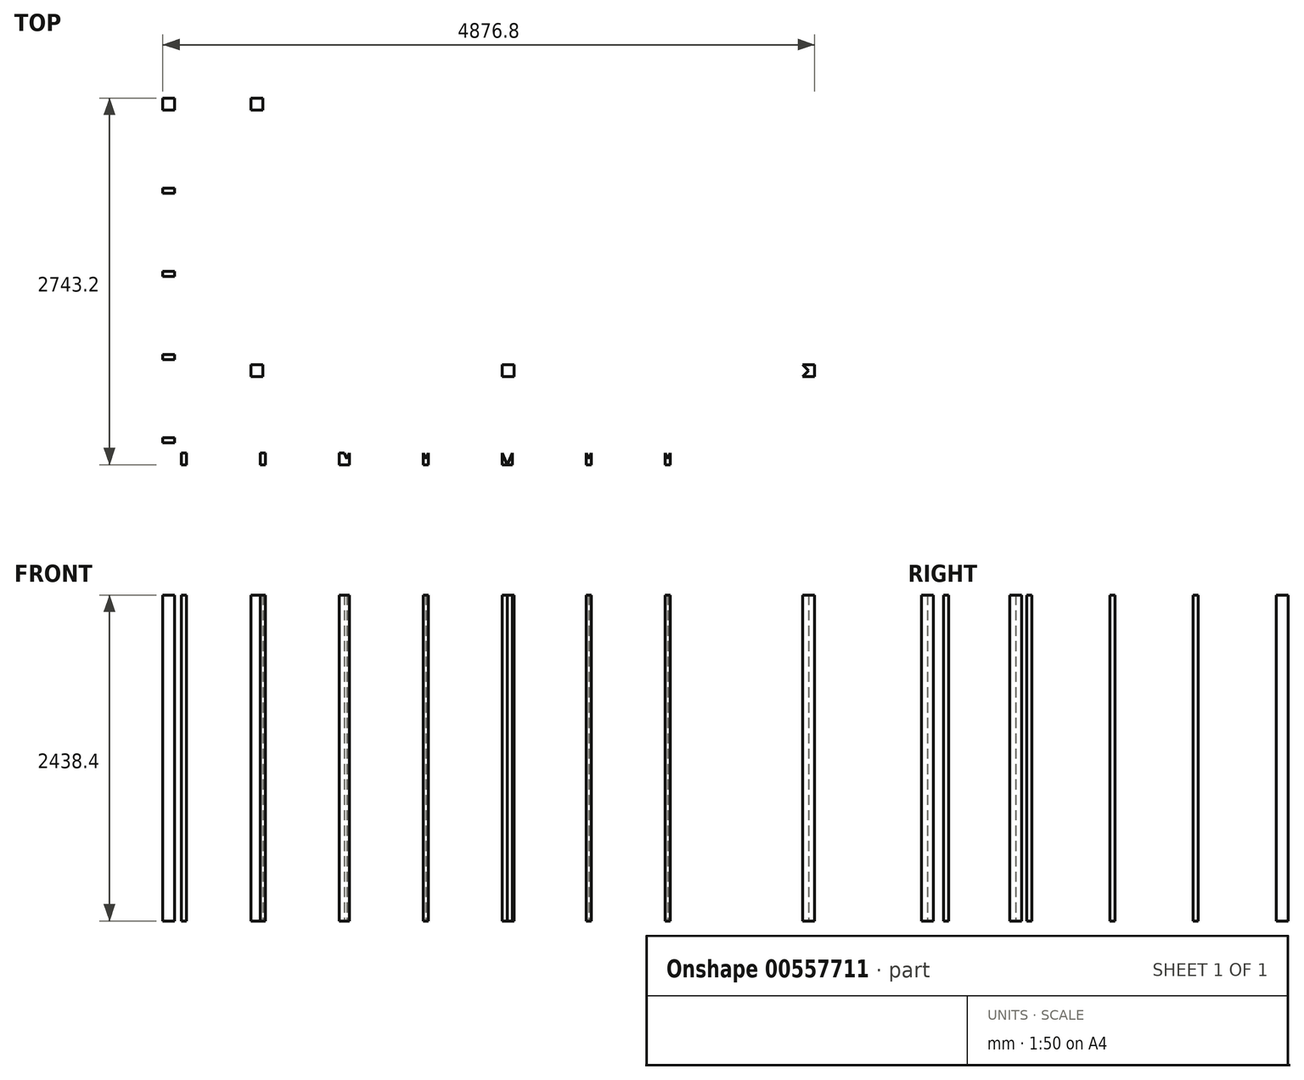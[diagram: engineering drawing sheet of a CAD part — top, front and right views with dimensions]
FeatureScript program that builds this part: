
annotation { "Feature Type Name" : "Feature", "Feature Type Description" : "" }
export const myFeature = defineFeature(function(context is Context, id is Id, definition is map)
    precondition{}
    {
        {
            var Q0;
            Q0=qCreatedBy(makeId("Top.planeOp"),FACE);
            var sketch = newSketch(context, id + "F0", { "sketchPlane" : qUnion([Q0])});
            skLineSegment(sketch, "E0.bottom", {"start": v(-518.2, -3048.88) * mm, "end": v(-518.2, -3086.98) * mm});
            skLineSegment(sketch, "E0.top", {"start": v(-429.3, -3048.88) * mm, "end": v(-429.3, -3086.98) * mm});
            skLineSegment(sketch, "E0.left", {"start": v(-518.2, -3048.88) * mm, "end": v(-429.3, -3048.88) * mm});
            skLineSegment(sketch, "E0.right", {"start": v(-518.2, -3086.98) * mm, "end": v(-429.3, -3086.98) * mm});
            skLineSegment(sketch, "E1", {"start": v(-518.2, -3086.98) * mm, "end": v(-429.3, -3048.88) * mm});
            skLineSegment(sketch, "E2", {"start": v(-518.2, -3048.88) * mm, "end": v(-429.3, -3086.98) * mm});
            skLineSegment(sketch, "E3.bottom", {"start": v(0, -673.1) * mm, "end": v(0, -711.2) * mm});
            skLineSegment(sketch, "E3.top", {"start": v(88.9, -673.1) * mm, "end": v(88.9, -711.2) * mm});
            skLineSegment(sketch, "E3.left", {"start": v(0, -673.1) * mm, "end": v(88.9, -673.1) * mm});
            skLineSegment(sketch, "E3.right", {"start": v(0, -711.2) * mm, "end": v(88.9, -711.2) * mm});
            skLineSegment(sketch, "E4", {"start": v(0, -711.2) * mm, "end": v(88.9, -673.1) * mm});
            skLineSegment(sketch, "E5", {"start": v(0, -673.1) * mm, "end": v(88.9, -711.2) * mm});
            skLineSegment(sketch, "E6.bottom", {"start": v(-839.1, -3188.58) * mm, "end": v(-839.1, -3277.48) * mm});
            skLineSegment(sketch, "E6.top", {"start": v(-801, -3188.58) * mm, "end": v(-801, -3277.48) * mm});
            skLineSegment(sketch, "E6.left", {"start": v(-839.1, -3188.58) * mm, "end": v(-801, -3188.58) * mm});
            skLineSegment(sketch, "E6.right", {"start": v(-839.1, -3277.48) * mm, "end": v(-801, -3277.48) * mm});
            skLineSegment(sketch, "E7", {"start": v(-839.1, -3277.48) * mm, "end": v(-801, -3188.58) * mm});
            skLineSegment(sketch, "E8", {"start": v(-839.1, -3188.58) * mm, "end": v(-801, -3277.48) * mm});
            skLineSegment(sketch, "E9.bottom", {"start": v(139.7, -2654.3) * mm, "end": v(139.7, -2743.2) * mm});
            skLineSegment(sketch, "E9.top", {"start": v(177.8, -2654.3) * mm, "end": v(177.8, -2743.2) * mm});
            skLineSegment(sketch, "E9.left", {"start": v(139.7, -2654.3) * mm, "end": v(177.8, -2654.3) * mm});
            skLineSegment(sketch, "E9.right", {"start": v(139.7, -2743.2) * mm, "end": v(177.8, -2743.2) * mm});
            skLineSegment(sketch, "E10", {"start": v(139.7, -2743.2) * mm, "end": v(177.8, -2654.3) * mm});
            skLineSegment(sketch, "E11", {"start": v(139.7, -2654.3) * mm, "end": v(177.8, -2743.2) * mm});
            skLineSegment(sketch, "E12.0.1.0", {"start": v(730.25, -2654.3) * mm, "end": v(730.25, -2743.2) * mm});
            skLineSegment(sketch, "E12.0.1.1", {"start": v(730.25, -2743.2) * mm, "end": v(768.35, -2654.3) * mm});
            skLineSegment(sketch, "E12.0.1.2", {"start": v(730.25, -2654.3) * mm, "end": v(768.35, -2654.3) * mm});
            skLineSegment(sketch, "E12.0.1.3", {"start": v(730.25, -2743.2) * mm, "end": v(768.35, -2743.2) * mm});
            skLineSegment(sketch, "E12.0.1.4", {"start": v(730.25, -2654.3) * mm, "end": v(768.35, -2743.2) * mm});
            skLineSegment(sketch, "E12.0.1.5", {"start": v(768.35, -2654.3) * mm, "end": v(768.35, -2743.2) * mm});
            skLineSegment(sketch, "E12.0.2.0", {"start": v(1320.8, -2654.3) * mm, "end": v(1320.8, -2743.2) * mm});
            skLineSegment(sketch, "E12.0.2.1", {"start": v(1320.8, -2743.2) * mm, "end": v(1358.9, -2654.3) * mm});
            skLineSegment(sketch, "E12.0.2.2", {"start": v(1320.8, -2654.3) * mm, "end": v(1358.9, -2654.3) * mm});
            skLineSegment(sketch, "E12.0.2.3", {"start": v(1320.8, -2743.2) * mm, "end": v(1358.9, -2743.2) * mm});
            skLineSegment(sketch, "E12.0.2.4", {"start": v(1320.8, -2654.3) * mm, "end": v(1358.9, -2743.2) * mm});
            skLineSegment(sketch, "E12.0.2.5", {"start": v(1358.9, -2654.3) * mm, "end": v(1358.9, -2743.2) * mm});
            skLineSegment(sketch, "E12.direction1", {"start": v(177.8, -2792) * mm, "end": v(177.8, -2743.2) * mm, "construction": true});
            skLineSegment(sketch, "E12.direction2", {"start": v(177.8, -2743.2) * mm, "end": v(768.35, -2743.2) * mm, "construction": true});
            skLineSegment(sketch, "E13.bottom", {"start": v(139.7, -2654.3) * mm, "end": v(139.7, -2641.6) * mm});
            skLineSegment(sketch, "E13.top", {"start": v(1358.9, -2654.3) * mm, "end": v(1358.9, -2641.6) * mm});
            skLineSegment(sketch, "E13.left", {"start": v(139.7, -2654.3) * mm, "end": v(1358.9, -2654.3) * mm});
            skLineSegment(sketch, "E13.right", {"start": v(139.7, -2641.6) * mm, "end": v(1358.9, -2641.6) * mm});
            skLineSegment(sketch, "E14.0.1.0", {"start": v(1949.45, -2654.3) * mm, "end": v(1987.55, -2743.2) * mm});
            skLineSegment(sketch, "E14.0.1.1", {"start": v(1358.9, -2654.3) * mm, "end": v(2578.1, -2654.3) * mm});
            skLineSegment(sketch, "E14.0.1.2", {"start": v(2540, -2654.3) * mm, "end": v(2540, -2743.2) * mm});
            skLineSegment(sketch, "E14.0.1.3", {"start": v(1358.9, -2641.6) * mm, "end": v(2578.1, -2641.6) * mm});
            skLineSegment(sketch, "E14.0.1.4", {"start": v(1397, -2743.2) * mm, "end": v(1987.55, -2743.2) * mm, "construction": true});
            skLineSegment(sketch, "E14.0.1.5", {"start": v(1987.55, -2654.3) * mm, "end": v(1987.55, -2743.2) * mm});
            skLineSegment(sketch, "E14.0.1.6", {"start": v(1949.45, -2654.3) * mm, "end": v(1949.45, -2743.2) * mm});
            skLineSegment(sketch, "E14.0.1.8", {"start": v(2540, -2743.2) * mm, "end": v(2578.1, -2654.3) * mm});
            skLineSegment(sketch, "E14.0.1.9", {"start": v(2578.1, -2654.3) * mm, "end": v(2578.1, -2743.2) * mm});
            skLineSegment(sketch, "E14.0.1.10", {"start": v(1949.45, -2743.2) * mm, "end": v(1987.55, -2654.3) * mm});
            skLineSegment(sketch, "E14.0.1.11", {"start": v(2540, -2654.3) * mm, "end": v(2578.1, -2743.2) * mm});
            skLineSegment(sketch, "E14.0.1.12", {"start": v(1358.9, -2654.3) * mm, "end": v(1397, -2743.2) * mm});
            skLineSegment(sketch, "E14.0.1.13", {"start": v(1397, -2654.3) * mm, "end": v(1397, -2743.2) * mm});
            skLineSegment(sketch, "E14.0.1.14", {"start": v(1358.9, -2743.2) * mm, "end": v(1397, -2654.3) * mm});
            skLineSegment(sketch, "E14.0.1.15", {"start": v(1949.45, -2654.3) * mm, "end": v(1987.55, -2654.3) * mm});
            skLineSegment(sketch, "E14.0.1.16", {"start": v(1949.45, -2743.2) * mm, "end": v(1987.55, -2743.2) * mm});
            skLineSegment(sketch, "E14.0.1.17", {"start": v(1358.9, -2654.3) * mm, "end": v(1397, -2654.3) * mm});
            skLineSegment(sketch, "E14.0.1.18", {"start": v(2540, -2654.3) * mm, "end": v(2578.1, -2654.3) * mm});
            skLineSegment(sketch, "E14.0.1.19", {"start": v(2540, -2743.2) * mm, "end": v(2578.1, -2743.2) * mm});
            skLineSegment(sketch, "E14.0.1.20", {"start": v(1358.9, -2743.2) * mm, "end": v(1397, -2743.2) * mm});
            skLineSegment(sketch, "E14.0.1.22", {"start": v(2578.1, -2654.3) * mm, "end": v(2578.1, -2641.6) * mm});
            skLineSegment(sketch, "E14.0.1.23", {"start": v(1397, -2792) * mm, "end": v(1397, -2743.2) * mm, "construction": true});
            skLineSegment(sketch, "E14.0.2.0", {"start": v(3168.65, -2654.3) * mm, "end": v(3206.75, -2743.2) * mm});
            skLineSegment(sketch, "E14.0.2.1", {"start": v(2578.1, -2654.3) * mm, "end": v(3797.3, -2654.3) * mm});
            skLineSegment(sketch, "E14.0.2.2", {"start": v(3759.2, -2654.3) * mm, "end": v(3759.2, -2743.2) * mm});
            skLineSegment(sketch, "E14.0.2.3", {"start": v(2578.1, -2641.6) * mm, "end": v(3797.3, -2641.6) * mm});
            skLineSegment(sketch, "E14.0.2.4", {"start": v(2616.2, -2743.2) * mm, "end": v(3206.75, -2743.2) * mm, "construction": true});
            skLineSegment(sketch, "E14.0.2.5", {"start": v(3206.75, -2654.3) * mm, "end": v(3206.75, -2743.2) * mm});
            skLineSegment(sketch, "E14.0.2.6", {"start": v(3168.65, -2654.3) * mm, "end": v(3168.65, -2743.2) * mm});
            skLineSegment(sketch, "E14.0.2.7", {"start": v(2578.1, -2654.3) * mm, "end": v(2578.1, -2743.2) * mm});
            skLineSegment(sketch, "E14.0.2.8", {"start": v(3759.2, -2743.2) * mm, "end": v(3797.3, -2654.3) * mm});
            skLineSegment(sketch, "E14.0.2.9", {"start": v(3797.3, -2654.3) * mm, "end": v(3797.3, -2743.2) * mm});
            skLineSegment(sketch, "E14.0.2.10", {"start": v(3168.65, -2743.2) * mm, "end": v(3206.75, -2654.3) * mm});
            skLineSegment(sketch, "E14.0.2.11", {"start": v(3759.2, -2654.3) * mm, "end": v(3797.3, -2743.2) * mm});
            skLineSegment(sketch, "E14.0.2.12", {"start": v(2578.1, -2654.3) * mm, "end": v(2616.2, -2743.2) * mm});
            skLineSegment(sketch, "E14.0.2.13", {"start": v(2616.2, -2654.3) * mm, "end": v(2616.2, -2743.2) * mm});
            skLineSegment(sketch, "E14.0.2.14", {"start": v(2578.1, -2743.2) * mm, "end": v(2616.2, -2654.3) * mm});
            skLineSegment(sketch, "E14.0.2.15", {"start": v(3168.65, -2654.3) * mm, "end": v(3206.75, -2654.3) * mm});
            skLineSegment(sketch, "E14.0.2.16", {"start": v(3168.65, -2743.2) * mm, "end": v(3206.75, -2743.2) * mm});
            skLineSegment(sketch, "E14.0.2.17", {"start": v(2578.1, -2654.3) * mm, "end": v(2616.2, -2654.3) * mm});
            skLineSegment(sketch, "E14.0.2.18", {"start": v(3759.2, -2654.3) * mm, "end": v(3797.3, -2654.3) * mm});
            skLineSegment(sketch, "E14.0.2.19", {"start": v(3759.2, -2743.2) * mm, "end": v(3797.3, -2743.2) * mm});
            skLineSegment(sketch, "E14.0.2.20", {"start": v(2578.1, -2743.2) * mm, "end": v(2616.2, -2743.2) * mm});
            skLineSegment(sketch, "E14.0.2.21", {"start": v(2578.1, -2654.3) * mm, "end": v(2578.1, -2641.6) * mm});
            skLineSegment(sketch, "E14.0.2.22", {"start": v(3797.3, -2654.3) * mm, "end": v(3797.3, -2641.6) * mm});
            skLineSegment(sketch, "E14.0.2.23", {"start": v(2616.2, -2792) * mm, "end": v(2616.2, -2743.2) * mm, "construction": true});
            skLineSegment(sketch, "E14.direction1", {"start": v(1358.9, -2743.2) * mm, "end": v(1358.9, -2667) * mm, "construction": true});
            skLineSegment(sketch, "E14.direction2", {"start": v(1358.9, -2743.2) * mm, "end": v(2578.1, -2743.2) * mm, "construction": true});
            skCircle(sketch, "E15", {"center": v(4876.8, -2804.36) * mm, "radius": 228.6 * mm});
            skLineSegment(sketch, "E16.bottom", {"start": v(660.4, 0) * mm, "end": v(749.3, 0) * mm});
            skLineSegment(sketch, "E16.top", {"start": v(660.4, -88.9) * mm, "end": v(749.3, -88.9) * mm});
            skLineSegment(sketch, "E16.left", {"start": v(660.4, 0) * mm, "end": v(660.4, -88.9) * mm});
            skLineSegment(sketch, "E16.right", {"start": v(749.3, 0) * mm, "end": v(749.3, -88.9) * mm});
            skLineSegment(sketch, "E17", {"start": v(660.4, -88.9) * mm, "end": v(749.3, 0) * mm});
            skLineSegment(sketch, "E18", {"start": v(660.4, 0) * mm, "end": v(749.3, -88.9) * mm});
            skLineSegment(sketch, "E19.bottom", {"start": v(2540, -1993.9) * mm, "end": v(2628.9, -1993.9) * mm});
            skLineSegment(sketch, "E19.top", {"start": v(2540, -2082.8) * mm, "end": v(2628.9, -2082.8) * mm});
            skLineSegment(sketch, "E19.left", {"start": v(2540, -1993.9) * mm, "end": v(2540, -2082.8) * mm});
            skLineSegment(sketch, "E19.right", {"start": v(2628.9, -1993.9) * mm, "end": v(2628.9, -2082.8) * mm});
            skLineSegment(sketch, "E20", {"start": v(2540, -2082.8) * mm, "end": v(2628.9, -1993.9) * mm});
            skLineSegment(sketch, "E21", {"start": v(2540, -1993.9) * mm, "end": v(2628.9, -2082.8) * mm});
            skLineSegment(sketch, "E22.bottom", {"start": v(6053.75, -1993.9) * mm, "end": v(6142.65, -1993.9) * mm});
            skLineSegment(sketch, "E22.top", {"start": v(6053.75, -2082.8) * mm, "end": v(6142.65, -2082.8) * mm});
            skLineSegment(sketch, "E22.left", {"start": v(6053.75, -1993.9) * mm, "end": v(6053.75, -2082.8) * mm});
            skLineSegment(sketch, "E22.right", {"start": v(6142.65, -1993.9) * mm, "end": v(6142.65, -2082.8) * mm});
            skLineSegment(sketch, "E23", {"start": v(6053.75, -2082.8) * mm, "end": v(6142.65, -1993.9) * mm});
            skLineSegment(sketch, "E24", {"start": v(6053.75, -1993.9) * mm, "end": v(6142.65, -2082.8) * mm});
            skLineSegment(sketch, "E25.bottom", {"start": v(114.3, -2628.9) * mm, "end": v(-114.3, -2628.9) * mm});
            skLineSegment(sketch, "E25.top", {"start": v(114.3, -2857.5) * mm, "end": v(-114.3, -2857.5) * mm});
            skLineSegment(sketch, "E25.left", {"start": v(114.3, -2628.9) * mm, "end": v(114.3, -2857.5) * mm});
            skLineSegment(sketch, "E25.right", {"start": v(-114.3, -2628.9) * mm, "end": v(-114.3, -2857.5) * mm});
            skLineSegment(sketch, "E26.bottom", {"start": v(4787.9, -1371.6) * mm, "end": v(4787.9, -1409.7) * mm});
            skLineSegment(sketch, "E26.top", {"start": v(4876.8, -1371.6) * mm, "end": v(4876.8, -1409.7) * mm});
            skLineSegment(sketch, "E26.left", {"start": v(4787.9, -1371.6) * mm, "end": v(4876.8, -1371.6) * mm});
            skLineSegment(sketch, "E26.right", {"start": v(4787.9, -1409.7) * mm, "end": v(4876.8, -1409.7) * mm});
            skLineSegment(sketch, "E27", {"start": v(4787.9, -1409.7) * mm, "end": v(4876.8, -1371.6) * mm});
            skLineSegment(sketch, "E28", {"start": v(4787.9, -1371.6) * mm, "end": v(4876.8, -1409.7) * mm});
            skLineSegment(sketch, "E29.bottom", {"start": v(4787.9, -571.5) * mm, "end": v(4787.9, -609.6) * mm});
            skLineSegment(sketch, "E29.top", {"start": v(4876.8, -571.5) * mm, "end": v(4876.8, -609.6) * mm});
            skLineSegment(sketch, "E29.left", {"start": v(4787.9, -571.5) * mm, "end": v(4876.8, -571.5) * mm});
            skLineSegment(sketch, "E29.right", {"start": v(4787.9, -609.6) * mm, "end": v(4876.8, -609.6) * mm});
            skLineSegment(sketch, "E30", {"start": v(4787.9, -609.6) * mm, "end": v(4876.8, -571.5) * mm});
            skLineSegment(sketch, "E31", {"start": v(4787.9, -571.5) * mm, "end": v(4876.8, -609.6) * mm});
            skLineSegment(sketch, "E32.bottom", {"start": v(5923.7, -2715.46) * mm, "end": v(5923.7, -2804.36) * mm});
            skLineSegment(sketch, "E32.top", {"start": v(5961.8, -2715.46) * mm, "end": v(5961.8, -2804.36) * mm});
            skLineSegment(sketch, "E32.left", {"start": v(5923.7, -2715.46) * mm, "end": v(5961.8, -2715.46) * mm});
            skLineSegment(sketch, "E32.right", {"start": v(5923.7, -2804.36) * mm, "end": v(5961.8, -2804.36) * mm});
            skLineSegment(sketch, "E33", {"start": v(5923.7, -2804.36) * mm, "end": v(5961.8, -2715.46) * mm});
            skLineSegment(sketch, "E34", {"start": v(5923.7, -2715.46) * mm, "end": v(5961.8, -2804.36) * mm});
            skLineSegment(sketch, "E35.bottom", {"start": v(4787.9, -1638.3) * mm, "end": v(4787.9, -1676.4) * mm});
            skLineSegment(sketch, "E35.top", {"start": v(4876.8, -1638.3) * mm, "end": v(4876.8, -1676.4) * mm});
            skLineSegment(sketch, "E35.left", {"start": v(4787.9, -1638.3) * mm, "end": v(4876.8, -1638.3) * mm});
            skLineSegment(sketch, "E35.right", {"start": v(4787.9, -1676.4) * mm, "end": v(4876.8, -1676.4) * mm});
            skLineSegment(sketch, "E36", {"start": v(4787.9, -1676.4) * mm, "end": v(4876.8, -1638.3) * mm});
            skLineSegment(sketch, "E37", {"start": v(4787.9, -1638.3) * mm, "end": v(4876.8, -1676.4) * mm});
            skLineSegment(sketch, "E38.bottom", {"start": v(7014.46, -3056.69) * mm, "end": v(7204.96, -3056.69) * mm});
            skLineSegment(sketch, "E38.top", {"start": v(6442.96, -3818.69) * mm, "end": v(7103.36, -3818.69) * mm});
            skLineSegment(sketch, "E38.left", {"start": v(6442.96, -3628.19) * mm, "end": v(6442.96, -3818.69) * mm});
            skLineSegment(sketch, "E38.right", {"start": v(7204.96, -3056.69) * mm, "end": v(7204.96, -3717.09) * mm});
            skLineSegment(sketch, "E39", {"start": v(6442.96, -3628.19) * mm, "end": v(7014.46, -3056.69) * mm});
            skLineSegment(sketch, "E40", {"start": v(7204.96, -3717.09) * mm, "end": v(7103.36, -3818.69) * mm});
            skLineSegment(sketch, "E41.bottom", {"start": v(4554.32, -1919.19) * mm, "end": v(4744.82, -1919.19) * mm});
            skLineSegment(sketch, "E41.top", {"start": v(3982.82, -2681.19) * mm, "end": v(4643.22, -2681.19) * mm});
            skLineSegment(sketch, "E41.left", {"start": v(3982.82, -2490.69) * mm, "end": v(3982.82, -2681.19) * mm});
            skLineSegment(sketch, "E41.right", {"start": v(4744.82, -1919.19) * mm, "end": v(4744.82, -2579.59) * mm});
            skLineSegment(sketch, "E42", {"start": v(3982.82, -2490.69) * mm, "end": v(4554.32, -1919.19) * mm});
            skLineSegment(sketch, "E43", {"start": v(4744.82, -2579.59) * mm, "end": v(4643.22, -2681.19) * mm});
            skLineSegment(sketch, "E44.bottom", {"start": v(4787.9, 0) * mm, "end": v(4787.9, -38.1) * mm});
            skLineSegment(sketch, "E44.top", {"start": v(4876.8, 0) * mm, "end": v(4876.8, -38.1) * mm});
            skLineSegment(sketch, "E44.left", {"start": v(4787.9, 0) * mm, "end": v(4876.8, 0) * mm});
            skLineSegment(sketch, "E44.right", {"start": v(4787.9, -38.1) * mm, "end": v(4876.8, -38.1) * mm});
            skLineSegment(sketch, "E45", {"start": v(4787.9, -38.1) * mm, "end": v(4876.8, 0) * mm});
            skLineSegment(sketch, "E46", {"start": v(4787.9, 0) * mm, "end": v(4876.8, -38.1) * mm});
            skLineSegment(sketch, "E47.bottom", {"start": v(0, 0) * mm, "end": v(88.9, 0) * mm});
            skLineSegment(sketch, "E47.top", {"start": v(0, -88.9) * mm, "end": v(88.9, -88.9) * mm});
            skLineSegment(sketch, "E47.left", {"start": v(0, 0) * mm, "end": v(0, -88.9) * mm});
            skLineSegment(sketch, "E47.right", {"start": v(88.9, 0) * mm, "end": v(88.9, -88.9) * mm});
            skLineSegment(sketch, "E48", {"start": v(0, -88.9) * mm, "end": v(88.9, 0) * mm});
            skLineSegment(sketch, "E49", {"start": v(0, 0) * mm, "end": v(88.9, -88.9) * mm});
            skLineSegment(sketch, "E50", {"start": v(-1165.05, -2735.16) * mm, "end": v(-1073.4, -2444.46) * mm});
            skLineSegment(sketch, "E51", {"start": v(-1073.4, -2444.46) * mm, "end": v(-1049.17, -2452.1) * mm});
            skLineSegment(sketch, "E52", {"start": v(-1049.17, -2452.1) * mm, "end": v(-1140.82, -2742.8) * mm});
            skLineSegment(sketch, "E53", {"start": v(-1140.82, -2742.8) * mm, "end": v(-1165.05, -2735.16) * mm});
            skLineSegment(sketch, "E54", {"start": v(-1140.82, -2742.8) * mm, "end": v(-1049.17, -3033.49) * mm});
            skLineSegment(sketch, "E55", {"start": v(-1049.17, -3033.49) * mm, "end": v(-1073.4, -3041.13) * mm});
            skLineSegment(sketch, "E56", {"start": v(-1073.4, -3041.13) * mm, "end": v(-1165.05, -2750.43) * mm});
            skLineSegment(sketch, "E57", {"start": v(-1165.05, -2750.43) * mm, "end": v(-1140.82, -2742.8) * mm});
            skLineSegment(sketch, "E58", {"start": v(-1165.05, -2735.16) * mm, "end": v(-1165.05, -2750.43) * mm});
            skLineSegment(sketch, "E59", {"start": v(-1140.82, -2742.8) * mm, "end": v(-1165.05, -2742.8) * mm, "construction": true});
            skLineSegment(sketch, "E60", {"start": v(0, -370.85) * mm, "end": v(91.66, -80.16) * mm});
            skLineSegment(sketch, "E61", {"start": v(91.66, -80.16) * mm, "end": v(115.88, -87.8) * mm});
            skLineSegment(sketch, "E62", {"start": v(115.88, -87.8) * mm, "end": v(24.22, -378.5) * mm});
            skLineSegment(sketch, "E63", {"start": v(24.22, -378.5) * mm, "end": v(0, -370.85) * mm});
            skLineSegment(sketch, "E64", {"start": v(24.22, -378.5) * mm, "end": v(115.88, -669.19) * mm});
            skLineSegment(sketch, "E65", {"start": v(115.88, -669.19) * mm, "end": v(91.66, -676.82) * mm});
            skLineSegment(sketch, "E66", {"start": v(91.66, -676.82) * mm, "end": v(0, -386.13) * mm});
            skLineSegment(sketch, "E67", {"start": v(0, -386.13) * mm, "end": v(24.22, -378.5) * mm});
            skLineSegment(sketch, "E68", {"start": v(0, -370.85) * mm, "end": v(0, -386.13) * mm});
            skLineSegment(sketch, "E69", {"start": v(24.22, -378.5) * mm, "end": v(0, -378.5) * mm, "construction": true});
            skLineSegment(sketch, "E70.bottom", {"start": v(0, -1295.4) * mm, "end": v(0, -1333.5) * mm});
            skLineSegment(sketch, "E70.top", {"start": v(88.9, -1295.4) * mm, "end": v(88.9, -1333.5) * mm});
            skLineSegment(sketch, "E70.left", {"start": v(0, -1295.4) * mm, "end": v(88.9, -1295.4) * mm});
            skLineSegment(sketch, "E70.right", {"start": v(0, -1333.5) * mm, "end": v(88.9, -1333.5) * mm});
            skLineSegment(sketch, "E71", {"start": v(0, -1333.5) * mm, "end": v(88.9, -1295.4) * mm});
            skLineSegment(sketch, "E72", {"start": v(0, -1295.4) * mm, "end": v(88.9, -1333.5) * mm});
            skLineSegment(sketch, "E73.bottom", {"start": v(0, -1917.7) * mm, "end": v(0, -1955.8) * mm});
            skLineSegment(sketch, "E73.top", {"start": v(88.9, -1917.7) * mm, "end": v(88.9, -1955.8) * mm});
            skLineSegment(sketch, "E73.left", {"start": v(0, -1917.7) * mm, "end": v(88.9, -1917.7) * mm});
            skLineSegment(sketch, "E73.right", {"start": v(0, -1955.8) * mm, "end": v(88.9, -1955.8) * mm});
            skLineSegment(sketch, "E74", {"start": v(0, -1955.8) * mm, "end": v(88.9, -1917.7) * mm});
            skLineSegment(sketch, "E75", {"start": v(0, -1917.7) * mm, "end": v(88.9, -1955.8) * mm});
            skLineSegment(sketch, "E76.bottom", {"start": v(0, -2540) * mm, "end": v(0, -2578.1) * mm});
            skLineSegment(sketch, "E76.top", {"start": v(88.9, -2540) * mm, "end": v(88.9, -2578.1) * mm});
            skLineSegment(sketch, "E76.left", {"start": v(0, -2540) * mm, "end": v(88.9, -2540) * mm});
            skLineSegment(sketch, "E76.right", {"start": v(0, -2578.1) * mm, "end": v(88.9, -2578.1) * mm});
            skLineSegment(sketch, "E77", {"start": v(0, -2578.1) * mm, "end": v(88.9, -2540) * mm});
            skLineSegment(sketch, "E78", {"start": v(0, -2540) * mm, "end": v(88.9, -2578.1) * mm});
            skLineSegment(sketch, "E79.0.1.0", {"start": v(0, -993.15) * mm, "end": v(91.66, -702.46) * mm});
            skLineSegment(sketch, "E79.0.1.1", {"start": v(115.88, -710.1) * mm, "end": v(24.22, -1000.8) * mm});
            skLineSegment(sketch, "E79.0.1.2", {"start": v(24.22, -1000.8) * mm, "end": v(115.88, -1291.49) * mm});
            skLineSegment(sketch, "E79.0.1.3", {"start": v(91.66, -1299.12) * mm, "end": v(0, -1008.43) * mm});
            skLineSegment(sketch, "E79.0.1.4", {"start": v(24.22, -1000.8) * mm, "end": v(0, -993.15) * mm});
            skLineSegment(sketch, "E79.0.1.5", {"start": v(0, -1008.43) * mm, "end": v(24.22, -1000.8) * mm});
            skLineSegment(sketch, "E79.0.1.6", {"start": v(91.66, -702.46) * mm, "end": v(115.88, -710.1) * mm});
            skLineSegment(sketch, "E79.0.1.7", {"start": v(115.88, -1291.49) * mm, "end": v(91.66, -1299.12) * mm});
            skLineSegment(sketch, "E79.0.2.0", {"start": v(0, -1615.45) * mm, "end": v(91.66, -1324.76) * mm});
            skLineSegment(sketch, "E79.0.2.1", {"start": v(115.88, -1332.4) * mm, "end": v(24.22, -1623.1) * mm});
            skLineSegment(sketch, "E79.0.2.2", {"start": v(24.22, -1623.1) * mm, "end": v(115.88, -1913.79) * mm});
            skLineSegment(sketch, "E79.0.2.3", {"start": v(91.66, -1921.42) * mm, "end": v(0, -1630.73) * mm});
            skLineSegment(sketch, "E79.0.2.4", {"start": v(24.22, -1623.1) * mm, "end": v(0, -1615.45) * mm});
            skLineSegment(sketch, "E79.0.2.5", {"start": v(0, -1630.73) * mm, "end": v(24.22, -1623.1) * mm});
            skLineSegment(sketch, "E79.0.2.6", {"start": v(91.66, -1324.76) * mm, "end": v(115.88, -1332.4) * mm});
            skLineSegment(sketch, "E79.0.2.7", {"start": v(115.88, -1913.79) * mm, "end": v(91.66, -1921.42) * mm});
            skLineSegment(sketch, "E79.0.3.0", {"start": v(0, -2237.75) * mm, "end": v(91.66, -1947.06) * mm});
            skLineSegment(sketch, "E79.0.3.1", {"start": v(115.88, -1954.7) * mm, "end": v(24.22, -2245.4) * mm});
            skLineSegment(sketch, "E79.0.3.2", {"start": v(24.22, -2245.4) * mm, "end": v(115.88, -2536.09) * mm});
            skLineSegment(sketch, "E79.0.3.3", {"start": v(91.66, -2543.72) * mm, "end": v(0, -2253.03) * mm});
            skLineSegment(sketch, "E79.0.3.4", {"start": v(24.22, -2245.4) * mm, "end": v(0, -2237.75) * mm});
            skLineSegment(sketch, "E79.0.3.5", {"start": v(0, -2253.03) * mm, "end": v(24.22, -2245.4) * mm});
            skLineSegment(sketch, "E79.0.3.6", {"start": v(91.66, -1947.06) * mm, "end": v(115.88, -1954.7) * mm});
            skLineSegment(sketch, "E79.0.3.7", {"start": v(115.88, -2536.09) * mm, "end": v(91.66, -2543.72) * mm});
            skLineSegment(sketch, "E79.direction1", {"start": v(91.66, -676.82) * mm, "end": v(117.06, -676.82) * mm, "construction": true});
            skLineSegment(sketch, "E79.direction2", {"start": v(91.66, -676.82) * mm, "end": v(91.66, -1299.12) * mm, "construction": true});
            skLineSegment(sketch, "E80.bottom", {"start": v(107.95, -25.4) * mm, "end": v(641.35, -25.4) * mm});
            skLineSegment(sketch, "E80.top", {"start": v(107.95, -63.5) * mm, "end": v(641.35, -63.5) * mm});
            skLineSegment(sketch, "E80.left", {"start": v(107.95, -25.4) * mm, "end": v(107.95, -63.5) * mm});
            skLineSegment(sketch, "E80.right", {"start": v(641.35, -25.4) * mm, "end": v(641.35, -63.5) * mm});
            skLineSegment(sketch, "E81.bottom", {"start": v(685.8, -107.95) * mm, "end": v(723.9, -107.95) * mm});
            skLineSegment(sketch, "E81.top", {"start": v(685.8, -1974.85) * mm, "end": v(723.9, -1974.85) * mm});
            skLineSegment(sketch, "E81.left", {"start": v(685.8, -107.95) * mm, "end": v(685.8, -1974.85) * mm});
            skLineSegment(sketch, "E81.right", {"start": v(723.9, -107.95) * mm, "end": v(723.9, -1974.85) * mm});
            skLineSegment(sketch, "E82.bottom", {"start": v(660.4, -1993.9) * mm, "end": v(749.3, -1993.9) * mm});
            skLineSegment(sketch, "E82.top", {"start": v(660.4, -2082.8) * mm, "end": v(749.3, -2082.8) * mm});
            skLineSegment(sketch, "E82.left", {"start": v(660.4, -1993.9) * mm, "end": v(660.4, -2082.8) * mm});
            skLineSegment(sketch, "E82.right", {"start": v(749.3, -1993.9) * mm, "end": v(749.3, -2082.8) * mm});
            skLineSegment(sketch, "E83", {"start": v(660.4, -2082.8) * mm, "end": v(749.3, -1993.9) * mm});
            skLineSegment(sketch, "E84", {"start": v(660.4, -1993.9) * mm, "end": v(749.3, -2082.8) * mm});
            skLineSegment(sketch, "E85.bottom", {"start": v(768.35, -2057.4) * mm, "end": v(2520.95, -2057.4) * mm});
            skLineSegment(sketch, "E85.top", {"start": v(768.35, -2019.3) * mm, "end": v(2520.95, -2019.3) * mm});
            skLineSegment(sketch, "E85.left", {"start": v(768.35, -2057.4) * mm, "end": v(768.35, -2019.3) * mm});
            skLineSegment(sketch, "E85.right", {"start": v(2520.95, -2057.4) * mm, "end": v(2520.95, -2019.3) * mm});
            skLineSegment(sketch, "E86.bottom", {"start": v(685.8, -419.1) * mm, "end": v(127, -419.1) * mm});
            skLineSegment(sketch, "E86.top", {"start": v(685.8, -381) * mm, "end": v(127, -381) * mm});
            skLineSegment(sketch, "E86.left", {"start": v(685.8, -419.1) * mm, "end": v(685.8, -381) * mm});
            skLineSegment(sketch, "E86.right", {"start": v(127, -419.1) * mm, "end": v(127, -381) * mm});
            skLineSegment(sketch, "E87.bottom", {"start": v(127, -723.9) * mm, "end": v(685.8, -723.9) * mm});
            skLineSegment(sketch, "E87.top", {"start": v(127, -762) * mm, "end": v(685.8, -762) * mm});
            skLineSegment(sketch, "E87.left", {"start": v(127, -723.9) * mm, "end": v(127, -762) * mm});
            skLineSegment(sketch, "E87.right", {"start": v(685.8, -723.9) * mm, "end": v(685.8, -762) * mm});
            skLineSegment(sketch, "E88.bottom", {"start": v(127, -1041.4) * mm, "end": v(685.8, -1041.4) * mm});
            skLineSegment(sketch, "E88.top", {"start": v(127, -1079.5) * mm, "end": v(685.8, -1079.5) * mm});
            skLineSegment(sketch, "E88.left", {"start": v(127, -1041.4) * mm, "end": v(127, -1079.5) * mm});
            skLineSegment(sketch, "E88.right", {"start": v(685.8, -1041.4) * mm, "end": v(685.8, -1079.5) * mm});
            skLineSegment(sketch, "E89.bottom", {"start": v(127, -1397) * mm, "end": v(685.8, -1397) * mm});
            skLineSegment(sketch, "E89.top", {"start": v(127, -1358.9) * mm, "end": v(685.8, -1358.9) * mm});
            skLineSegment(sketch, "E89.left", {"start": v(127, -1358.9) * mm, "end": v(127, -1397) * mm});
            skLineSegment(sketch, "E89.right", {"start": v(685.8, -1358.9) * mm, "end": v(685.8, -1397) * mm});
            skLineSegment(sketch, "E90.bottom", {"start": v(127, -1676.4) * mm, "end": v(685.8, -1676.4) * mm});
            skLineSegment(sketch, "E90.top", {"start": v(127, -1714.5) * mm, "end": v(685.8, -1714.5) * mm});
            skLineSegment(sketch, "E90.left", {"start": v(127, -1676.4) * mm, "end": v(127, -1714.5) * mm});
            skLineSegment(sketch, "E90.right", {"start": v(685.8, -1676.4) * mm, "end": v(685.8, -1714.5) * mm});
            skLineSegment(sketch, "E91.bottom", {"start": v(127, -2057.4) * mm, "end": v(641.35, -2057.4) * mm});
            skLineSegment(sketch, "E91.top", {"start": v(127, -2019.3) * mm, "end": v(641.35, -2019.3) * mm});
            skLineSegment(sketch, "E91.left", {"start": v(127, -2019.3) * mm, "end": v(127, -2057.4) * mm});
            skLineSegment(sketch, "E91.right", {"start": v(641.35, -2019.3) * mm, "end": v(641.35, -2057.4) * mm});
            skLineSegment(sketch, "E92.bottom", {"start": v(2565.4, -2101.85) * mm, "end": v(2603.5, -2101.85) * mm});
            skLineSegment(sketch, "E92.top", {"start": v(2565.4, -2622.55) * mm, "end": v(2603.5, -2622.55) * mm});
            skLineSegment(sketch, "E92.left", {"start": v(2565.4, -2101.85) * mm, "end": v(2565.4, -2622.55) * mm});
            skLineSegment(sketch, "E92.right", {"start": v(2603.5, -2101.85) * mm, "end": v(2603.5, -2622.55) * mm});
            skLineSegment(sketch, "E93.bottom", {"start": v(1320.8, -2057.4) * mm, "end": v(1358.9, -2057.4) * mm});
            skLineSegment(sketch, "E93.top", {"start": v(1320.8, -2622.55) * mm, "end": v(1358.9, -2622.55) * mm});
            skLineSegment(sketch, "E93.left", {"start": v(1320.8, -2057.4) * mm, "end": v(1320.8, -2622.55) * mm});
            skLineSegment(sketch, "E93.right", {"start": v(1358.9, -2057.4) * mm, "end": v(1358.9, -2622.55) * mm});
            skLineSegment(sketch, "E94.bottom", {"start": v(1003.3, -2057.4) * mm, "end": v(1041.4, -2057.4) * mm});
            skLineSegment(sketch, "E94.top", {"start": v(1003.3, -2622.55) * mm, "end": v(1041.4, -2622.55) * mm});
            skLineSegment(sketch, "E94.left", {"start": v(1003.3, -2057.4) * mm, "end": v(1003.3, -2622.55) * mm});
            skLineSegment(sketch, "E94.right", {"start": v(1041.4, -2057.4) * mm, "end": v(1041.4, -2622.55) * mm});
            skLineSegment(sketch, "E95.bottom", {"start": v(685.8, -2101.85) * mm, "end": v(723.9, -2101.85) * mm});
            skLineSegment(sketch, "E95.top", {"start": v(685.8, -2622.55) * mm, "end": v(723.9, -2622.55) * mm});
            skLineSegment(sketch, "E95.left", {"start": v(685.8, -2101.85) * mm, "end": v(685.8, -2622.55) * mm});
            skLineSegment(sketch, "E95.right", {"start": v(723.9, -2101.85) * mm, "end": v(723.9, -2622.55) * mm});
            skLineSegment(sketch, "E96.bottom", {"start": v(127, -2374.9) * mm, "end": v(685.8, -2374.9) * mm});
            skLineSegment(sketch, "E96.top", {"start": v(127, -2336.8) * mm, "end": v(685.8, -2336.8) * mm});
            skLineSegment(sketch, "E96.left", {"start": v(127, -2336.8) * mm, "end": v(127, -2374.9) * mm});
            skLineSegment(sketch, "E96.right", {"start": v(685.8, -2336.8) * mm, "end": v(685.8, -2374.9) * mm});
            skLineSegment(sketch, "E97.bottom", {"start": v(-530.02, -3378.46) * mm, "end": v(-441.12, -3378.46) * mm});
            skLineSegment(sketch, "E97.top", {"start": v(-530.02, -3359.4) * mm, "end": v(-441.12, -3359.4) * mm});
            skLineSegment(sketch, "E97.left", {"start": v(-530.02, -3378.46) * mm, "end": v(-530.02, -3359.4) * mm});
            skLineSegment(sketch, "E97.right", {"start": v(-441.12, -3378.46) * mm, "end": v(-441.12, -3359.4) * mm});
            skLineSegment(sketch, "E98", {"start": v(-530.02, -3359.4) * mm, "end": v(-441.12, -3378.46) * mm});
            skLineSegment(sketch, "E99", {"start": v(-441.12, -3359.4) * mm, "end": v(-530.02, -3378.46) * mm});
            skLineSegment(sketch, "E100.bottom", {"start": v(660.4, -107.95) * mm, "end": v(749.3, -107.95) * mm});
            skLineSegment(sketch, "E100.left", {"start": v(660.4, -107.95) * mm, "end": v(660.4, -88.9) * mm});
            skLineSegment(sketch, "E100.right", {"start": v(749.3, -107.95) * mm, "end": v(749.3, -88.9) * mm});
            skLineSegment(sketch, "E101", {"start": v(660.4, -88.9) * mm, "end": v(749.3, -107.95) * mm});
            skLineSegment(sketch, "E102", {"start": v(749.3, -88.9) * mm, "end": v(660.4, -107.95) * mm});
            skLineSegment(sketch, "E103.top", {"start": v(660.4, -1974.85) * mm, "end": v(749.3, -1974.85) * mm});
            skLineSegment(sketch, "E103.left", {"start": v(660.4, -1993.9) * mm, "end": v(660.4, -1974.85) * mm});
            skLineSegment(sketch, "E103.right", {"start": v(749.3, -1993.9) * mm, "end": v(749.3, -1974.85) * mm});
            skLineSegment(sketch, "E104", {"start": v(660.4, -1974.85) * mm, "end": v(749.3, -1993.9) * mm});
            skLineSegment(sketch, "E105", {"start": v(749.3, -1974.85) * mm, "end": v(660.4, -1993.9) * mm});
            skLineSegment(sketch, "E106.bottom", {"start": v(641.35, 0) * mm, "end": v(641.35, -88.9) * mm});
            skLineSegment(sketch, "E106.left", {"start": v(641.35, 0) * mm, "end": v(660.4, 0) * mm});
            skLineSegment(sketch, "E106.right", {"start": v(641.35, -88.9) * mm, "end": v(660.4, -88.9) * mm});
            skLineSegment(sketch, "E107", {"start": v(660.4, 0) * mm, "end": v(641.35, -88.9) * mm});
            skLineSegment(sketch, "E108", {"start": v(660.4, -88.9) * mm, "end": v(641.35, 0) * mm});
            skLineSegment(sketch, "E109.top", {"start": v(107.95, 0) * mm, "end": v(107.95, -88.9) * mm});
            skLineSegment(sketch, "E109.left", {"start": v(88.9, 0) * mm, "end": v(107.95, 0) * mm});
            skLineSegment(sketch, "E109.right", {"start": v(88.9, -88.9) * mm, "end": v(107.95, -88.9) * mm});
            skLineSegment(sketch, "E110", {"start": v(107.95, 0) * mm, "end": v(88.9, -88.9) * mm});
            skLineSegment(sketch, "E111", {"start": v(107.95, -88.9) * mm, "end": v(88.9, 0) * mm});
            skLineSegment(sketch, "E112.top", {"start": v(768.35, -1993.9) * mm, "end": v(768.35, -2082.8) * mm});
            skLineSegment(sketch, "E112.left", {"start": v(749.3, -1993.9) * mm, "end": v(768.35, -1993.9) * mm});
            skLineSegment(sketch, "E112.right", {"start": v(749.3, -2082.8) * mm, "end": v(768.35, -2082.8) * mm});
            skLineSegment(sketch, "E113", {"start": v(768.35, -1993.9) * mm, "end": v(749.3, -2082.8) * mm});
            skLineSegment(sketch, "E114", {"start": v(768.35, -2082.8) * mm, "end": v(749.3, -1993.9) * mm});
            skLineSegment(sketch, "E115.bottom", {"start": v(2540, -2101.85) * mm, "end": v(2628.9, -2101.85) * mm});
            skLineSegment(sketch, "E115.left", {"start": v(2540, -2101.85) * mm, "end": v(2540, -2082.8) * mm});
            skLineSegment(sketch, "E115.right", {"start": v(2628.9, -2101.85) * mm, "end": v(2628.9, -2082.8) * mm});
            skLineSegment(sketch, "E116", {"start": v(2540, -2082.8) * mm, "end": v(2628.9, -2101.85) * mm});
            skLineSegment(sketch, "E117", {"start": v(2628.9, -2082.8) * mm, "end": v(2540, -2101.85) * mm});
            skLineSegment(sketch, "E118.bottom", {"start": v(2520.95, -1993.9) * mm, "end": v(2520.95, -2082.8) * mm});
            skLineSegment(sketch, "E118.left", {"start": v(2520.95, -1993.9) * mm, "end": v(2540, -1993.9) * mm});
            skLineSegment(sketch, "E118.right", {"start": v(2520.95, -2082.8) * mm, "end": v(2540, -2082.8) * mm});
            skLineSegment(sketch, "E119", {"start": v(2540, -1993.9) * mm, "end": v(2520.95, -2082.8) * mm});
            skLineSegment(sketch, "E120", {"start": v(2540, -2082.8) * mm, "end": v(2520.95, -1993.9) * mm});
            skLineSegment(sketch, "E121.top", {"start": v(2647.95, -1993.9) * mm, "end": v(2647.95, -2082.8) * mm});
            skLineSegment(sketch, "E121.left", {"start": v(2628.9, -1993.9) * mm, "end": v(2647.95, -1993.9) * mm});
            skLineSegment(sketch, "E121.right", {"start": v(2628.9, -2082.8) * mm, "end": v(2647.95, -2082.8) * mm});
            skLineSegment(sketch, "E122", {"start": v(2647.95, -1993.9) * mm, "end": v(2628.9, -2082.8) * mm});
            skLineSegment(sketch, "E123", {"start": v(2647.95, -2082.8) * mm, "end": v(2628.9, -1993.9) * mm});
            skLineSegment(sketch, "E124.bottom", {"start": v(641.35, -1993.9) * mm, "end": v(641.35, -2082.8) * mm});
            skLineSegment(sketch, "E124.left", {"start": v(641.35, -1993.9) * mm, "end": v(660.4, -1993.9) * mm});
            skLineSegment(sketch, "E124.right", {"start": v(641.35, -2082.8) * mm, "end": v(660.4, -2082.8) * mm});
            skLineSegment(sketch, "E125", {"start": v(660.4, -1993.9) * mm, "end": v(641.35, -2082.8) * mm});
            skLineSegment(sketch, "E126", {"start": v(660.4, -2082.8) * mm, "end": v(641.35, -1993.9) * mm});
            skLineSegment(sketch, "E127.bottom", {"start": v(660.4, -2101.85) * mm, "end": v(749.3, -2101.85) * mm});
            skLineSegment(sketch, "E127.left", {"start": v(660.4, -2101.85) * mm, "end": v(660.4, -2082.8) * mm});
            skLineSegment(sketch, "E127.right", {"start": v(749.3, -2101.85) * mm, "end": v(749.3, -2082.8) * mm});
            skLineSegment(sketch, "E128", {"start": v(660.4, -2082.8) * mm, "end": v(749.3, -2101.85) * mm});
            skLineSegment(sketch, "E129", {"start": v(749.3, -2082.8) * mm, "end": v(660.4, -2101.85) * mm});
            skLineSegment(sketch, "E130.bottom", {"start": v(1308.1, -2641.6) * mm, "end": v(1397, -2641.6) * mm});
            skLineSegment(sketch, "E130.top", {"start": v(1308.1, -2622.55) * mm, "end": v(1397, -2622.55) * mm});
            skLineSegment(sketch, "E130.left", {"start": v(1308.1, -2641.6) * mm, "end": v(1308.1, -2622.55) * mm});
            skLineSegment(sketch, "E130.right", {"start": v(1397, -2641.6) * mm, "end": v(1397, -2622.55) * mm});
            skLineSegment(sketch, "E131", {"start": v(1308.1, -2622.55) * mm, "end": v(1397, -2641.6) * mm});
            skLineSegment(sketch, "E132", {"start": v(1397, -2622.55) * mm, "end": v(1308.1, -2641.6) * mm});
            skLineSegment(sketch, "E133.bottom", {"start": v(88.9, -356.8) * mm, "end": v(88.9, -445.7) * mm});
            skLineSegment(sketch, "E133.top", {"start": v(127, -356.8) * mm, "end": v(127, -445.7) * mm});
            skLineSegment(sketch, "E133.left", {"start": v(88.9, -356.8) * mm, "end": v(127, -356.8) * mm});
            skLineSegment(sketch, "E133.right", {"start": v(88.9, -445.7) * mm, "end": v(127, -445.7) * mm});
            skLineSegment(sketch, "E134", {"start": v(88.9, -445.7) * mm, "end": v(127, -356.8) * mm});
            skLineSegment(sketch, "E135", {"start": v(88.9, -356.8) * mm, "end": v(127, -445.7) * mm});
            skLineSegment(sketch, "E136.bottom", {"start": v(2540, -2641.6) * mm, "end": v(2628.9, -2641.6) * mm});
            skLineSegment(sketch, "E136.top", {"start": v(2540, -2622.55) * mm, "end": v(2628.9, -2622.55) * mm});
            skLineSegment(sketch, "E136.left", {"start": v(2540, -2641.6) * mm, "end": v(2540, -2622.55) * mm});
            skLineSegment(sketch, "E136.right", {"start": v(2628.9, -2641.6) * mm, "end": v(2628.9, -2622.55) * mm});
            skLineSegment(sketch, "E137", {"start": v(2540, -2622.55) * mm, "end": v(2628.9, -2641.6) * mm});
            skLineSegment(sketch, "E138", {"start": v(2628.9, -2622.55) * mm, "end": v(2540, -2641.6) * mm});
            skLineSegment(sketch, "E139.bottom", {"start": v(1638.3, -2057.4) * mm, "end": v(1676.4, -2057.4) * mm});
            skLineSegment(sketch, "E139.top", {"start": v(1638.3, -2622.55) * mm, "end": v(1676.4, -2622.55) * mm});
            skLineSegment(sketch, "E139.left", {"start": v(1638.3, -2057.4) * mm, "end": v(1638.3, -2622.55) * mm});
            skLineSegment(sketch, "E139.right", {"start": v(1676.4, -2057.4) * mm, "end": v(1676.4, -2622.55) * mm});
            skLineSegment(sketch, "E140.bottom", {"start": v(1955.8, -2057.4) * mm, "end": v(1993.9, -2057.4) * mm});
            skLineSegment(sketch, "E140.top", {"start": v(1955.8, -2622.55) * mm, "end": v(1993.9, -2622.55) * mm});
            skLineSegment(sketch, "E140.left", {"start": v(1955.8, -2057.4) * mm, "end": v(1955.8, -2622.55) * mm});
            skLineSegment(sketch, "E140.right", {"start": v(1993.9, -2057.4) * mm, "end": v(1993.9, -2622.55) * mm});
            skLineSegment(sketch, "E141.bottom", {"start": v(2273.3, -2057.4) * mm, "end": v(2311.4, -2057.4) * mm});
            skLineSegment(sketch, "E141.top", {"start": v(2273.3, -2622.55) * mm, "end": v(2311.4, -2622.55) * mm});
            skLineSegment(sketch, "E141.left", {"start": v(2273.3, -2057.4) * mm, "end": v(2273.3, -2622.55) * mm});
            skLineSegment(sketch, "E141.right", {"start": v(2311.4, -2057.4) * mm, "end": v(2311.4, -2622.55) * mm});
            skLineSegment(sketch, "E142.bottom", {"start": v(4787.9, -1993.9) * mm, "end": v(4876.8, -1993.9) * mm});
            skLineSegment(sketch, "E142.top", {"start": v(4787.9, -2082.8) * mm, "end": v(4876.8, -2082.8) * mm});
            skLineSegment(sketch, "E142.left", {"start": v(4787.9, -1993.9) * mm, "end": v(4787.9, -2082.8) * mm});
            skLineSegment(sketch, "E142.right", {"start": v(4876.8, -1993.9) * mm, "end": v(4876.8, -2082.8) * mm});
            skLineSegment(sketch, "E143", {"start": v(4787.9, -2082.8) * mm, "end": v(4876.8, -1993.9) * mm});
            skLineSegment(sketch, "E144", {"start": v(4787.9, -1993.9) * mm, "end": v(4876.8, -2082.8) * mm});
            skLineSegment(sketch, "E145.bottom", {"start": v(4768.85, -2082.8) * mm, "end": v(4787.9, -2082.8) * mm});
            skLineSegment(sketch, "E145.top", {"start": v(4768.85, -1993.9) * mm, "end": v(4787.9, -1993.9) * mm});
            skLineSegment(sketch, "E145.left", {"start": v(4768.85, -2082.8) * mm, "end": v(4768.85, -1993.9) * mm});
            skLineSegment(sketch, "E145.right", {"start": v(4787.9, -2082.8) * mm, "end": v(4787.9, -1993.9) * mm});
            skLineSegment(sketch, "E146", {"start": v(4768.85, -1993.9) * mm, "end": v(4787.9, -2082.8) * mm});
            skLineSegment(sketch, "E147", {"start": v(4787.9, -1993.9) * mm, "end": v(4768.85, -2082.8) * mm});
            skLineSegment(sketch, "E148.bottom", {"start": v(2647.95, -2019.3) * mm, "end": v(4768.85, -2019.3) * mm});
            skLineSegment(sketch, "E148.top", {"start": v(2647.95, -2057.4) * mm, "end": v(4768.85, -2057.4) * mm});
            skLineSegment(sketch, "E148.left", {"start": v(2647.95, -2019.3) * mm, "end": v(2647.95, -2057.4) * mm});
            skLineSegment(sketch, "E148.right", {"start": v(4768.85, -2019.3) * mm, "end": v(4768.85, -2057.4) * mm});
            skLineSegment(sketch, "E149.bottom", {"start": v(2857.5, -2057.4) * mm, "end": v(2895.6, -2057.4) * mm});
            skLineSegment(sketch, "E149.top", {"start": v(2857.5, -2622.55) * mm, "end": v(2895.6, -2622.55) * mm});
            skLineSegment(sketch, "E149.left", {"start": v(2857.5, -2057.4) * mm, "end": v(2857.5, -2622.55) * mm});
            skLineSegment(sketch, "E149.right", {"start": v(2895.6, -2057.4) * mm, "end": v(2895.6, -2622.55) * mm});
            skLineSegment(sketch, "E150.bottom", {"start": v(3149.6, -2057.4) * mm, "end": v(3187.7, -2057.4) * mm});
            skLineSegment(sketch, "E150.top", {"start": v(3149.6, -2622.55) * mm, "end": v(3187.7, -2622.55) * mm});
            skLineSegment(sketch, "E150.left", {"start": v(3149.6, -2057.4) * mm, "end": v(3149.6, -2622.55) * mm});
            skLineSegment(sketch, "E150.right", {"start": v(3187.7, -2057.4) * mm, "end": v(3187.7, -2622.55) * mm});
            skLineSegment(sketch, "E151.bottom", {"start": v(3441.7, -2057.4) * mm, "end": v(3479.8, -2057.4) * mm});
            skLineSegment(sketch, "E151.top", {"start": v(3441.7, -2622.55) * mm, "end": v(3479.8, -2622.55) * mm});
            skLineSegment(sketch, "E151.left", {"start": v(3441.7, -2057.4) * mm, "end": v(3441.7, -2622.55) * mm});
            skLineSegment(sketch, "E151.right", {"start": v(3479.8, -2057.4) * mm, "end": v(3479.8, -2622.55) * mm});
            skLineSegment(sketch, "E152.bottom", {"start": v(3759.2, -2057.4) * mm, "end": v(3797.3, -2057.4) * mm});
            skLineSegment(sketch, "E152.top", {"start": v(3759.2, -2622.55) * mm, "end": v(3797.3, -2622.55) * mm});
            skLineSegment(sketch, "E152.left", {"start": v(3759.2, -2057.4) * mm, "end": v(3759.2, -2622.55) * mm});
            skLineSegment(sketch, "E152.right", {"start": v(3797.3, -2057.4) * mm, "end": v(3797.3, -2622.55) * mm});
            skSolve(sketch);
        }
        {
            var Q0;
            {var subQ0=sQuery(id+"F0.wireOp",EDGE,"E47.bottom");Q0=makeQuery(id+"F0.imprint","IMPRINT",FACE,{"disambiguationData":[TD([[makeQuery(id+"F0.imprint","IMPRINT",EDGE,{"derivedFrom":subQ0}),-1.0]])]});}
            var Q1;
            {var subQ0=sQuery(id+"F0.wireOp",EDGE,"E47.left");Q1=makeQuery(id+"F0.imprint","IMPRINT",FACE,{"disambiguationData":[TD([[makeQuery(id+"F0.imprint","IMPRINT",EDGE,{"derivedFrom":subQ0}),1.0]])]});}
            var Q2;
            {var subQ0=sQuery(id+"F0.wireOp",EDGE,"E47.top");Q2=makeQuery(id+"F0.imprint","IMPRINT",FACE,{"disambiguationData":[TD([[makeQuery(id+"F0.imprint","IMPRINT",EDGE,{"derivedFrom":subQ0}),1.0]])]});}
            var Q3;
            {var subQ0=sQuery(id+"F0.wireOp",EDGE,"E47.right");Q3=makeQuery(id+"F0.imprint","IMPRINT",FACE,{"disambiguationData":[TD([[makeQuery(id+"F0.imprint","IMPRINT",EDGE,{"derivedFrom":subQ0}),-1.0]])]});}
            var Q4;
            {var subQ0=sQuery(id+"F0.wireOp",EDGE,"E16.bottom");Q4=makeQuery(id+"F0.imprint","IMPRINT",FACE,{"disambiguationData":[TD([[makeQuery(id+"F0.imprint","IMPRINT",EDGE,{"derivedFrom":subQ0}),-1.0]])]});}
            var Q5;
            {var subQ0=sQuery(id+"F0.wireOp",EDGE,"E16.left");Q5=makeQuery(id+"F0.imprint","IMPRINT",FACE,{"disambiguationData":[TD([[makeQuery(id+"F0.imprint","IMPRINT",EDGE,{"derivedFrom":subQ0}),1.0]])]});}
            var Q6;
            {var subQ0=sQuery(id+"F0.wireOp",EDGE,"E16.top");Q6=makeQuery(id+"F0.imprint","IMPRINT",FACE,{"disambiguationData":[TD([[makeQuery(id+"F0.imprint","IMPRINT",EDGE,{"derivedFrom":subQ0}),1.0]])]});}
            var Q7;
            {var subQ0=sQuery(id+"F0.wireOp",EDGE,"E16.right");Q7=makeQuery(id+"F0.imprint","IMPRINT",FACE,{"disambiguationData":[TD([[makeQuery(id+"F0.imprint","IMPRINT",EDGE,{"derivedFrom":subQ0}),-1.0]])]});}
            var Q8;
            {var subQ0=sQuery(id+"F0.wireOp",EDGE,"E82.bottom");Q8=makeQuery(id+"F0.imprint","IMPRINT",FACE,{"disambiguationData":[TD([[makeQuery(id+"F0.imprint","IMPRINT",EDGE,{"derivedFrom":subQ0}),-1.0]])]});}
            var Q9;
            {var subQ0=sQuery(id+"F0.wireOp",EDGE,"E82.left");Q9=makeQuery(id+"F0.imprint","IMPRINT",FACE,{"disambiguationData":[TD([[makeQuery(id+"F0.imprint","IMPRINT",EDGE,{"derivedFrom":subQ0}),1.0]])]});}
            var Q10;
            {var subQ0=sQuery(id+"F0.wireOp",EDGE,"E82.top");Q10=makeQuery(id+"F0.imprint","IMPRINT",FACE,{"disambiguationData":[TD([[makeQuery(id+"F0.imprint","IMPRINT",EDGE,{"derivedFrom":subQ0}),1.0]])]});}
            var Q11;
            {var subQ0=sQuery(id+"F0.wireOp",EDGE,"E82.right");Q11=makeQuery(id+"F0.imprint","IMPRINT",FACE,{"disambiguationData":[TD([[makeQuery(id+"F0.imprint","IMPRINT",EDGE,{"derivedFrom":subQ0}),-1.0]])]});}
            var Q12;
            {var subQ0=sQuery(id+"F0.wireOp",EDGE,"E19.left");Q12=makeQuery(id+"F0.imprint","IMPRINT",FACE,{"disambiguationData":[TD([[makeQuery(id+"F0.imprint","IMPRINT",EDGE,{"derivedFrom":subQ0}),1.0]])]});}
            var Q13;
            {var subQ0=sQuery(id+"F0.wireOp",EDGE,"E19.bottom");Q13=makeQuery(id+"F0.imprint","IMPRINT",FACE,{"disambiguationData":[TD([[makeQuery(id+"F0.imprint","IMPRINT",EDGE,{"derivedFrom":subQ0}),-1.0]])]});}
            var Q14;
            {var subQ0=sQuery(id+"F0.wireOp",EDGE,"E19.right");Q14=makeQuery(id+"F0.imprint","IMPRINT",FACE,{"disambiguationData":[TD([[makeQuery(id+"F0.imprint","IMPRINT",EDGE,{"derivedFrom":subQ0}),-1.0]])]});}
            var Q15;
            {var subQ0=sQuery(id+"F0.wireOp",EDGE,"E19.top");Q15=makeQuery(id+"F0.imprint","IMPRINT",FACE,{"disambiguationData":[TD([[makeQuery(id+"F0.imprint","IMPRINT",EDGE,{"derivedFrom":subQ0}),1.0]])]});}
            var Q16;
            {var subQ0=sQuery(id+"F0.wireOp",EDGE,"E145.right");Q16=makeQuery(id+"F0.imprint","IMPRINT",FACE,{"disambiguationData":[TD([[makeQuery(id+"F0.imprint","IMPRINT",EDGE,{"derivedFrom":subQ0}),-1.0]])]});}
            var Q17;
            {var subQ0=sQuery(id+"F0.wireOp",EDGE,"E142.bottom");Q17=makeQuery(id+"F0.imprint","IMPRINT",FACE,{"disambiguationData":[TD([[makeQuery(id+"F0.imprint","IMPRINT",EDGE,{"derivedFrom":subQ0}),-1.0]])]});}
            var Q18;
            {var subQ0=sQuery(id+"F0.wireOp",EDGE,"E142.right");Q18=makeQuery(id+"F0.imprint","IMPRINT",FACE,{"disambiguationData":[TD([[makeQuery(id+"F0.imprint","IMPRINT",EDGE,{"derivedFrom":subQ0}),-1.0]])]});}
            var Q19;
            {var subQ0=sQuery(id+"F0.wireOp",EDGE,"E142.top");Q19=makeQuery(id+"F0.imprint","IMPRINT",FACE,{"disambiguationData":[TD([[makeQuery(id+"F0.imprint","IMPRINT",EDGE,{"derivedFrom":subQ0}),1.0]])]});}
            extrude(context, id + "F1", {"entities" : qUnion([Q0, Q1, Q2, Q3, Q4, Q5, Q6, Q7, Q8, Q9, Q10, Q11, Q12, Q13, Q14, Q15, Q16, Q17, Q18, Q19]), "depth" : 2438.4 * mm, "offsetDistance" : 25.4 * mm});
        }
        {
            var Q0;
            {var subQ0=sQuery(id+"F0.wireOp",EDGE,"E14.0.2.2");Q0=makeQuery(id+"F0.imprint","IMPRINT",FACE,{"disambiguationData":[TD([[makeQuery(id+"F0.imprint","IMPRINT",EDGE,{"derivedFrom":subQ0}),1.0]])]});}
            var Q1;
            {var subQ0=sQuery(id+"F0.wireOp",EDGE,"E14.0.2.18");Q1=makeQuery(id+"F0.imprint","IMPRINT",FACE,{"disambiguationData":[TD([[makeQuery(id+"F0.imprint","IMPRINT",EDGE,{"derivedFrom":subQ0}),-1.0]])]});}
            var Q2;
            {var subQ0=sQuery(id+"F0.wireOp",EDGE,"E14.0.2.19");Q2=makeQuery(id+"F0.imprint","IMPRINT",FACE,{"disambiguationData":[TD([[makeQuery(id+"F0.imprint","IMPRINT",EDGE,{"derivedFrom":subQ0}),1.0]])]});}
            var Q3;
            {var subQ0=sQuery(id+"F0.wireOp",EDGE,"E14.0.2.15");Q3=makeQuery(id+"F0.imprint","IMPRINT",FACE,{"disambiguationData":[TD([[makeQuery(id+"F0.imprint","IMPRINT",EDGE,{"derivedFrom":subQ0}),-1.0]])]});}
            var Q4;
            {var subQ0=sQuery(id+"F0.wireOp",EDGE,"E14.0.2.6");Q4=makeQuery(id+"F0.imprint","IMPRINT",FACE,{"disambiguationData":[TD([[makeQuery(id+"F0.imprint","IMPRINT",EDGE,{"derivedFrom":subQ0}),1.0]])]});}
            var Q5;
            {var subQ0=sQuery(id+"F0.wireOp",EDGE,"E14.0.2.16");Q5=makeQuery(id+"F0.imprint","IMPRINT",FACE,{"disambiguationData":[TD([[makeQuery(id+"F0.imprint","IMPRINT",EDGE,{"derivedFrom":subQ0}),1.0]])]});}
            var Q6;
            {var subQ0=sQuery(id+"F0.wireOp",EDGE,"E14.0.2.5");Q6=makeQuery(id+"F0.imprint","IMPRINT",FACE,{"disambiguationData":[TD([[makeQuery(id+"F0.imprint","IMPRINT",EDGE,{"derivedFrom":subQ0}),-1.0]])]});}
            var Q7;
            {var subQ0=sQuery(id+"F0.wireOp",EDGE,"E14.0.1.2");Q7=makeQuery(id+"F0.imprint","IMPRINT",FACE,{"disambiguationData":[TD([[makeQuery(id+"F0.imprint","IMPRINT",EDGE,{"derivedFrom":subQ0}),1.0]])]});}
            var Q8;
            {var subQ0=sQuery(id+"F0.wireOp",EDGE,"E14.0.1.18");Q8=makeQuery(id+"F0.imprint","IMPRINT",FACE,{"disambiguationData":[TD([[makeQuery(id+"F0.imprint","IMPRINT",EDGE,{"derivedFrom":subQ0}),-1.0]])]});}
            var Q9;
            {var subQ0=sQuery(id+"F0.wireOp",EDGE,"E14.0.2.17");Q9=makeQuery(id+"F0.imprint","IMPRINT",FACE,{"disambiguationData":[TD([[makeQuery(id+"F0.imprint","IMPRINT",EDGE,{"derivedFrom":subQ0}),-1.0]])]});}
            var Q10;
            {var subQ0=sQuery(id+"F0.wireOp",EDGE,"E14.0.2.13");Q10=makeQuery(id+"F0.imprint","IMPRINT",FACE,{"disambiguationData":[TD([[makeQuery(id+"F0.imprint","IMPRINT",EDGE,{"derivedFrom":subQ0}),-1.0]])]});}
            var Q11;
            {var subQ0=sQuery(id+"F0.wireOp",EDGE,"E14.0.2.20");Q11=makeQuery(id+"F0.imprint","IMPRINT",FACE,{"disambiguationData":[TD([[makeQuery(id+"F0.imprint","IMPRINT",EDGE,{"derivedFrom":subQ0}),1.0]])]});}
            var Q12;
            {var subQ0=sQuery(id+"F0.wireOp",EDGE,"E14.0.1.19");Q12=makeQuery(id+"F0.imprint","IMPRINT",FACE,{"disambiguationData":[TD([[makeQuery(id+"F0.imprint","IMPRINT",EDGE,{"derivedFrom":subQ0}),1.0]])]});}
            var Q13;
            {var subQ0=sQuery(id+"F0.wireOp",EDGE,"E14.0.2.7");Q13=makeQuery(id+"F0.imprint","IMPRINT",FACE,{"disambiguationData":[TD([[makeQuery(id+"F0.imprint","IMPRINT",EDGE,{"derivedFrom":subQ0}),1.0]])]});}
            var Q14;
            {var subQ0=sQuery(id+"F0.wireOp",EDGE,"E14.0.2.7");Q14=makeQuery(id+"F0.imprint","IMPRINT",FACE,{"disambiguationData":[TD([[makeQuery(id+"F0.imprint","IMPRINT",EDGE,{"derivedFrom":subQ0}),-1.0]])]});}
            var Q15;
            {var subQ0=sQuery(id+"F0.wireOp",EDGE,"E14.0.1.15");Q15=makeQuery(id+"F0.imprint","IMPRINT",FACE,{"disambiguationData":[TD([[makeQuery(id+"F0.imprint","IMPRINT",EDGE,{"derivedFrom":subQ0}),-1.0]])]});}
            var Q16;
            {var subQ0=sQuery(id+"F0.wireOp",EDGE,"E14.0.1.5");Q16=makeQuery(id+"F0.imprint","IMPRINT",FACE,{"disambiguationData":[TD([[makeQuery(id+"F0.imprint","IMPRINT",EDGE,{"derivedFrom":subQ0}),-1.0]])]});}
            var Q17;
            {var subQ0=sQuery(id+"F0.wireOp",EDGE,"E14.0.1.6");Q17=makeQuery(id+"F0.imprint","IMPRINT",FACE,{"disambiguationData":[TD([[makeQuery(id+"F0.imprint","IMPRINT",EDGE,{"derivedFrom":subQ0}),1.0]])]});}
            var Q18;
            {var subQ0=sQuery(id+"F0.wireOp",EDGE,"E14.0.1.16");Q18=makeQuery(id+"F0.imprint","IMPRINT",FACE,{"disambiguationData":[TD([[makeQuery(id+"F0.imprint","IMPRINT",EDGE,{"derivedFrom":subQ0}),1.0]])]});}
            var Q19;
            {var subQ0=sQuery(id+"F0.wireOp",EDGE,"E14.0.2.9");Q19=makeQuery(id+"F0.imprint","IMPRINT",FACE,{"disambiguationData":[TD([[makeQuery(id+"F0.imprint","IMPRINT",EDGE,{"derivedFrom":subQ0}),-1.0]])]});}
            var Q20;
            {var subQ0=sQuery(id+"F0.wireOp",EDGE,"E14.0.1.17");Q20=makeQuery(id+"F0.imprint","IMPRINT",FACE,{"disambiguationData":[TD([[makeQuery(id+"F0.imprint","IMPRINT",EDGE,{"derivedFrom":subQ0}),-1.0]])]});}
            var Q21;
            {var subQ1=sQuery(id+"F0.wireOp",EDGE,"E12.0.2.1");var subQ3=sQuery(id+"F0.wireOp",EDGE,"E12.0.2.4");var subQ4=makeQuery(id+"F0.imprint","INTERSECT",VERTEX,{"derivedFrom":[subQ1,subQ3]});Q21=makeQuery(id+"F0.imprint","IMPRINT",FACE,{"disambiguationData":[TD([[makeQuery(id+"F0.imprint","IMPRINT",EDGE,{"disambiguationData":[TD([[subQ4,1.0]])],"derivedFrom":subQ3}),1.0]])]});}
            var Q22;
            {var subQ0=sQuery(id+"F0.wireOp",EDGE,"E12.0.2.0");Q22=makeQuery(id+"F0.imprint","IMPRINT",FACE,{"disambiguationData":[TD([[makeQuery(id+"F0.imprint","IMPRINT",EDGE,{"derivedFrom":subQ0}),1.0]])]});}
            var Q23;
            {var subQ0=sQuery(id+"F0.wireOp",EDGE,"E12.0.2.5");Q23=makeQuery(id+"F0.imprint","IMPRINT",FACE,{"disambiguationData":[TD([[makeQuery(id+"F0.imprint","IMPRINT",EDGE,{"derivedFrom":subQ0}),-1.0]])]});}
            var Q24;
            {var subQ0=sQuery(id+"F0.wireOp",EDGE,"E12.0.2.5");Q24=makeQuery(id+"F0.imprint","IMPRINT",FACE,{"disambiguationData":[TD([[makeQuery(id+"F0.imprint","IMPRINT",EDGE,{"derivedFrom":subQ0}),1.0]])]});}
            var Q25;
            {var subQ0=sQuery(id+"F0.wireOp",EDGE,"E14.0.1.13");Q25=makeQuery(id+"F0.imprint","IMPRINT",FACE,{"disambiguationData":[TD([[makeQuery(id+"F0.imprint","IMPRINT",EDGE,{"derivedFrom":subQ0}),-1.0]])]});}
            var Q26;
            {var subQ0=sQuery(id+"F0.wireOp",EDGE,"E14.0.1.20");Q26=makeQuery(id+"F0.imprint","IMPRINT",FACE,{"disambiguationData":[TD([[makeQuery(id+"F0.imprint","IMPRINT",EDGE,{"derivedFrom":subQ0}),1.0]])]});}
            var Q27;
            {var subQ0=sQuery(id+"F0.wireOp",EDGE,"E12.0.2.3");Q27=makeQuery(id+"F0.imprint","IMPRINT",FACE,{"disambiguationData":[TD([[makeQuery(id+"F0.imprint","IMPRINT",EDGE,{"derivedFrom":subQ0}),1.0]])]});}
            var Q28;
            {var subQ1=sQuery(id+"F0.wireOp",EDGE,"E12.0.1.1");var subQ3=sQuery(id+"F0.wireOp",EDGE,"E12.0.1.4");var subQ4=makeQuery(id+"F0.imprint","INTERSECT",VERTEX,{"derivedFrom":[subQ1,subQ3]});Q28=makeQuery(id+"F0.imprint","IMPRINT",FACE,{"disambiguationData":[TD([[makeQuery(id+"F0.imprint","IMPRINT",EDGE,{"disambiguationData":[TD([[subQ4,-1.0]])],"derivedFrom":subQ1}),1.0]])]});}
            var Q29;
            {var subQ0=sQuery(id+"F0.wireOp",EDGE,"E12.0.1.5");Q29=makeQuery(id+"F0.imprint","IMPRINT",FACE,{"disambiguationData":[TD([[makeQuery(id+"F0.imprint","IMPRINT",EDGE,{"derivedFrom":subQ0}),-1.0]])]});}
            var Q30;
            {var subQ0=sQuery(id+"F0.wireOp",EDGE,"E12.0.1.0");Q30=makeQuery(id+"F0.imprint","IMPRINT",FACE,{"disambiguationData":[TD([[makeQuery(id+"F0.imprint","IMPRINT",EDGE,{"derivedFrom":subQ0}),1.0]])]});}
            var Q31;
            {var subQ0=sQuery(id+"F0.wireOp",EDGE,"E12.0.1.3");Q31=makeQuery(id+"F0.imprint","IMPRINT",FACE,{"disambiguationData":[TD([[makeQuery(id+"F0.imprint","IMPRINT",EDGE,{"derivedFrom":subQ0}),1.0]])]});}
            var Q32;
            {var subQ1=sQuery(id+"F0.wireOp",EDGE,"E10");var subQ3=sQuery(id+"F0.wireOp",EDGE,"E11");var subQ4=makeQuery(id+"F0.imprint","INTERSECT",VERTEX,{"derivedFrom":[subQ1,subQ3]});Q32=makeQuery(id+"F0.imprint","IMPRINT",FACE,{"disambiguationData":[TD([[makeQuery(id+"F0.imprint","IMPRINT",EDGE,{"disambiguationData":[TD([[subQ4,-1.0]])],"derivedFrom":subQ1}),1.0]])]});}
            var Q33;
            {var subQ0=sQuery(id+"F0.wireOp",EDGE,"E9.bottom");Q33=makeQuery(id+"F0.imprint","IMPRINT",FACE,{"disambiguationData":[TD([[makeQuery(id+"F0.imprint","IMPRINT",EDGE,{"derivedFrom":subQ0}),1.0]])]});}
            var Q34;
            {var subQ0=sQuery(id+"F0.wireOp",EDGE,"E9.right");Q34=makeQuery(id+"F0.imprint","IMPRINT",FACE,{"disambiguationData":[TD([[makeQuery(id+"F0.imprint","IMPRINT",EDGE,{"derivedFrom":subQ0}),1.0]])]});}
            var Q35;
            {var subQ0=sQuery(id+"F0.wireOp",EDGE,"E9.top");Q35=makeQuery(id+"F0.imprint","IMPRINT",FACE,{"disambiguationData":[TD([[makeQuery(id+"F0.imprint","IMPRINT",EDGE,{"derivedFrom":subQ0}),-1.0]])]});}
            var Q36;
            {var subQ0=sQuery(id+"F0.wireOp",EDGE,"E76.right");Q36=makeQuery(id+"F0.imprint","IMPRINT",FACE,{"disambiguationData":[TD([[makeQuery(id+"F0.imprint","IMPRINT",EDGE,{"derivedFrom":subQ0}),1.0]])]});}
            var Q37;
            {var subQ0=sQuery(id+"F0.wireOp",EDGE,"E76.left");Q37=makeQuery(id+"F0.imprint","IMPRINT",FACE,{"disambiguationData":[TD([[makeQuery(id+"F0.imprint","IMPRINT",EDGE,{"derivedFrom":subQ0}),-1.0]])]});}
            var Q38;
            {var subQ0=sQuery(id+"F0.wireOp",EDGE,"E76.top");Q38=makeQuery(id+"F0.imprint","IMPRINT",FACE,{"disambiguationData":[TD([[makeQuery(id+"F0.imprint","IMPRINT",EDGE,{"derivedFrom":subQ0}),-1.0]])]});}
            var Q39;
            {var subQ0=sQuery(id+"F0.wireOp",EDGE,"E76.bottom");Q39=makeQuery(id+"F0.imprint","IMPRINT",FACE,{"disambiguationData":[TD([[makeQuery(id+"F0.imprint","IMPRINT",EDGE,{"derivedFrom":subQ0}),1.0]])]});}
            var Q40;
            {var subQ0=sQuery(id+"F0.wireOp",EDGE,"E73.right");Q40=makeQuery(id+"F0.imprint","IMPRINT",FACE,{"disambiguationData":[TD([[makeQuery(id+"F0.imprint","IMPRINT",EDGE,{"derivedFrom":subQ0}),1.0]])]});}
            var Q41;
            {var subQ0=sQuery(id+"F0.wireOp",EDGE,"E73.top");Q41=makeQuery(id+"F0.imprint","IMPRINT",FACE,{"disambiguationData":[TD([[makeQuery(id+"F0.imprint","IMPRINT",EDGE,{"derivedFrom":subQ0}),-1.0]])]});}
            var Q42;
            {var subQ0=sQuery(id+"F0.wireOp",EDGE,"E73.bottom");Q42=makeQuery(id+"F0.imprint","IMPRINT",FACE,{"disambiguationData":[TD([[makeQuery(id+"F0.imprint","IMPRINT",EDGE,{"derivedFrom":subQ0}),1.0]])]});}
            var Q43;
            {var subQ0=sQuery(id+"F0.wireOp",EDGE,"E73.left");Q43=makeQuery(id+"F0.imprint","IMPRINT",FACE,{"disambiguationData":[TD([[makeQuery(id+"F0.imprint","IMPRINT",EDGE,{"derivedFrom":subQ0}),-1.0]])]});}
            var Q44;
            {var subQ0=sQuery(id+"F0.wireOp",EDGE,"E70.right");Q44=makeQuery(id+"F0.imprint","IMPRINT",FACE,{"disambiguationData":[TD([[makeQuery(id+"F0.imprint","IMPRINT",EDGE,{"derivedFrom":subQ0}),1.0]])]});}
            var Q45;
            {var subQ0=sQuery(id+"F0.wireOp",EDGE,"E70.top");Q45=makeQuery(id+"F0.imprint","IMPRINT",FACE,{"disambiguationData":[TD([[makeQuery(id+"F0.imprint","IMPRINT",EDGE,{"derivedFrom":subQ0}),-1.0]])]});}
            var Q46;
            {var subQ0=sQuery(id+"F0.wireOp",EDGE,"E70.bottom");Q46=makeQuery(id+"F0.imprint","IMPRINT",FACE,{"disambiguationData":[TD([[makeQuery(id+"F0.imprint","IMPRINT",EDGE,{"derivedFrom":subQ0}),1.0]])]});}
            var Q47;
            {var subQ0=sQuery(id+"F0.wireOp",EDGE,"E70.left");Q47=makeQuery(id+"F0.imprint","IMPRINT",FACE,{"disambiguationData":[TD([[makeQuery(id+"F0.imprint","IMPRINT",EDGE,{"derivedFrom":subQ0}),-1.0]])]});}
            var Q48;
            {var subQ0=sQuery(id+"F0.wireOp",EDGE,"E3.left");Q48=makeQuery(id+"F0.imprint","IMPRINT",FACE,{"disambiguationData":[TD([[makeQuery(id+"F0.imprint","IMPRINT",EDGE,{"derivedFrom":subQ0}),-1.0]])]});}
            var Q49;
            {var subQ0=sQuery(id+"F0.wireOp",EDGE,"E3.bottom");Q49=makeQuery(id+"F0.imprint","IMPRINT",FACE,{"disambiguationData":[TD([[makeQuery(id+"F0.imprint","IMPRINT",EDGE,{"derivedFrom":subQ0}),1.0]])]});}
            var Q50;
            {var subQ0=sQuery(id+"F0.wireOp",EDGE,"E3.top");Q50=makeQuery(id+"F0.imprint","IMPRINT",FACE,{"disambiguationData":[TD([[makeQuery(id+"F0.imprint","IMPRINT",EDGE,{"derivedFrom":subQ0}),-1.0]])]});}
            var Q51;
            {var subQ0=sQuery(id+"F0.wireOp",EDGE,"E3.right");Q51=makeQuery(id+"F0.imprint","IMPRINT",FACE,{"disambiguationData":[TD([[makeQuery(id+"F0.imprint","IMPRINT",EDGE,{"derivedFrom":subQ0}),1.0]])]});}
            extrude(context, id + "F2", {"entities" : qUnion([Q0, Q1, Q2, Q3, Q4, Q5, Q6, Q7, Q8, Q9, Q10, Q11, Q12, Q13, Q14, Q15, Q16, Q17, Q18, Q19, Q20, Q21, Q22, Q23, Q24, Q25, Q26, Q27, Q28, Q29, Q30, Q31, Q32, Q33, Q34, Q35, Q36, Q37, Q38, Q39, Q40, Q41, Q42, Q43, Q44, Q45, Q46, Q47, Q48, Q49, Q50, Q51]), "depth" : 2438.4 * mm, "offsetDistance" : 25.4 * mm});
        }
    });
